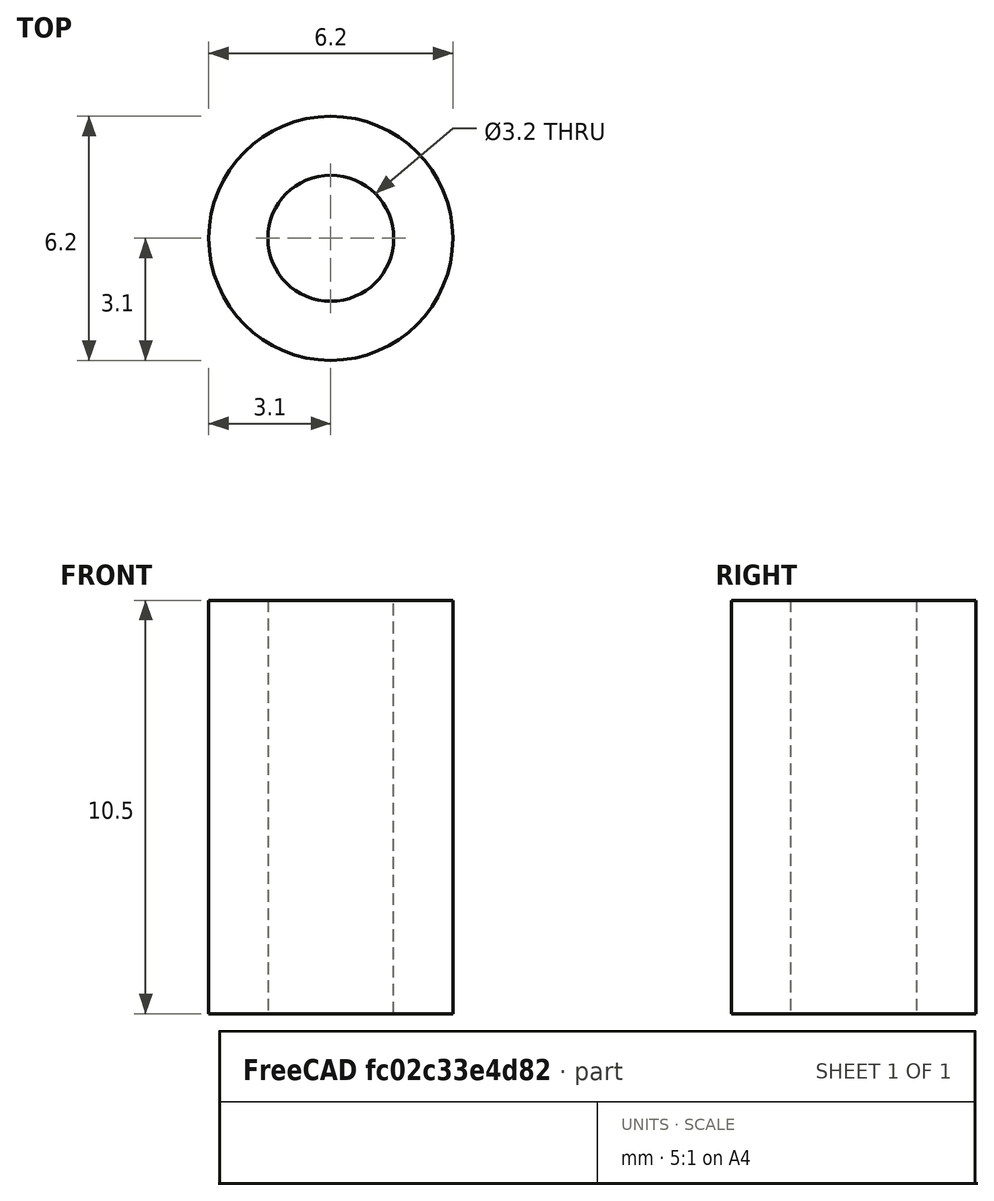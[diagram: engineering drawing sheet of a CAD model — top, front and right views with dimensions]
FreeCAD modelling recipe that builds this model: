
FCSTD DOCUMENT  (FreeCAD 0.20R29603 (Git))
Label: espacador-10mm5
License: All rights reserved
LicenseURL: http://en.wikipedia.org/wiki/All_rights_reserved
objects: Sketcher::SketchObject×1, PartDesign::Pad×1, PartDesign::Body×1
note: 4 computed .brp shape members not serialized (recipe doc carries the construction recipe); baked Part::Feature solids carry a one-line shape summary decoded from their .brp

FEATURE [Sketcher::SketchObject] Sketch
  FullyConstrained = true
  MapMode = 5
  Support = -> [XY_Plane]
  sketch-geometry (4):
    g0: Circle CenterX=0 CenterY=0 CenterZ=0 NormalX=0 NormalY=0 NormalZ=1 AngleXU=0 Radius=3.1
    g1: Circle CenterX=0 CenterY=0 CenterZ=0 NormalX=0 NormalY=0 NormalZ=1 AngleXU=0 Radius=1.6
    g2: GeomPoint X=3.1 Y=0 Z=0
    g3: GeomPoint X=1.6 Y=0 Z=0
  constraints (9):
    c: Coincident(g0,g-1)
    c: Coincident(g1,g0)
    c: Radius(g1) = 1.6
    c: PointOnObject(g3,g1)
    c: PointOnObject(g3,g-1)
    c: PointOnObject(g2,g0)
    c: PointOnObject(g2,g-1)
    c: DistanceX(g3,g2) = 1.5
    c: Radius(g0) = 3.1
FEATURE [PartDesign::Pad] Pad
  Direction = (0,0,1)
  Length = 10.5
  Length2 = 10
  Profile = -> Sketch
  ReferenceAxis = -> Sketch [N_Axis]
  Type = 0
FEATURE [PartDesign::Body] Body
  Group = -> [Sketch,Pad]
  Origin = -> Origin
  Tip = -> Pad
